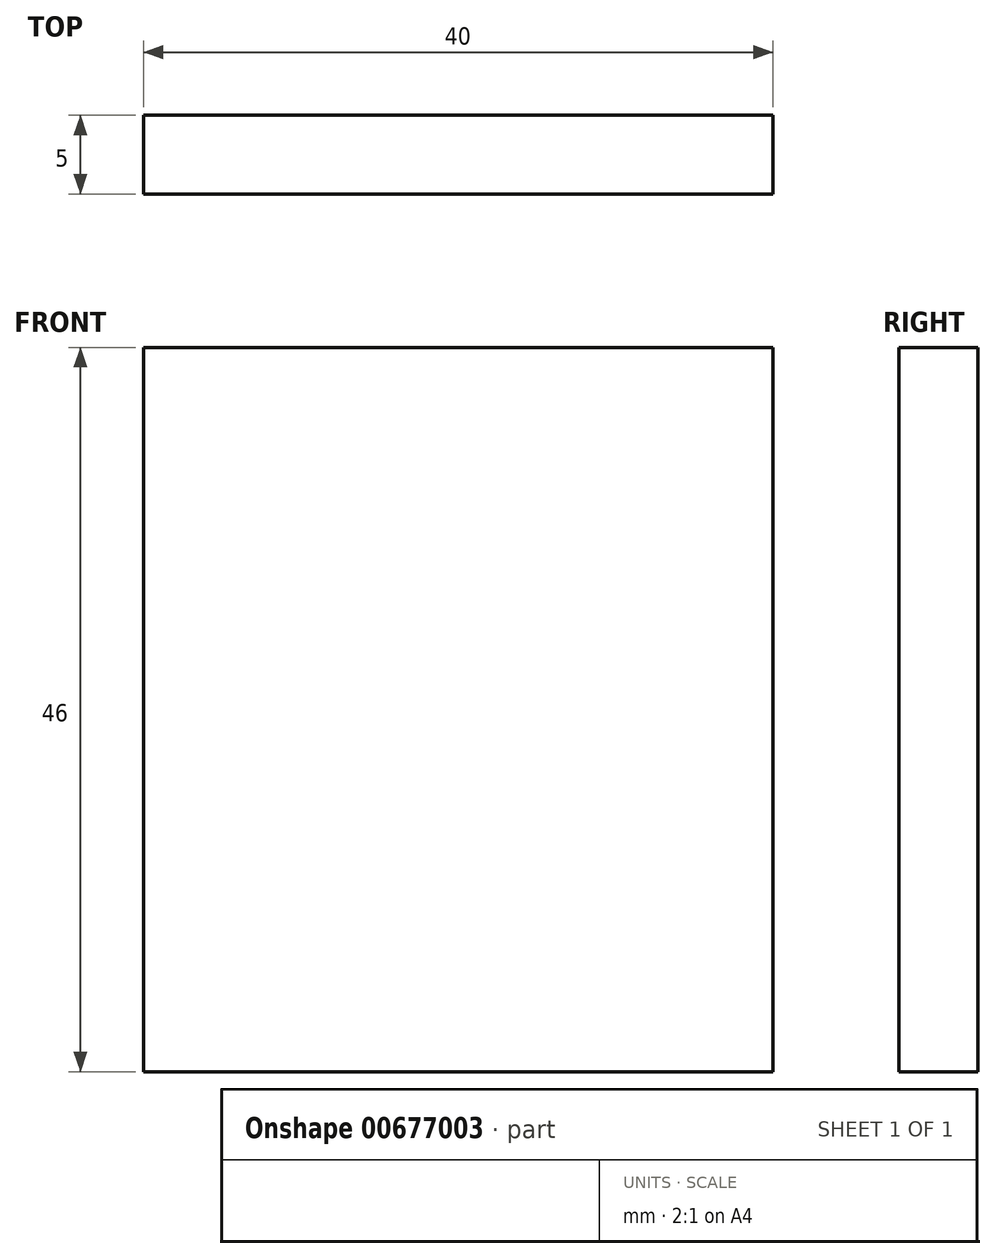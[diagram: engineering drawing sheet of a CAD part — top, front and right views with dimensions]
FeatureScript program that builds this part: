
annotation { "Feature Type Name" : "Feature", "Feature Type Description" : "" }
export const myFeature = defineFeature(function(context is Context, id is Id, definition is map)
    precondition{}
    {
        {
            var Q0;
            Q0=qCreatedBy(makeId("Front.planeOp"),FACE);
            var sketch = newSketch(context, id + "F0", { "sketchPlane" : qUnion([Q0])});
            skLineSegment(sketch, "E0.bottom", {"start": v(-20, 23) * mm, "end": v(20, 23) * mm});
            skLineSegment(sketch, "E0.top", {"start": v(-20, -23) * mm, "end": v(20, -23) * mm});
            skLineSegment(sketch, "E0.left", {"start": v(-20, 23) * mm, "end": v(-20, -23) * mm});
            skLineSegment(sketch, "E0.right", {"start": v(20, 23) * mm, "end": v(20, -23) * mm});
            skPoint(sketch, "E0.middle", {"position": v(0, 0) * mm});
            skSolve(sketch);
        }
        {
            var Q0;
            Q0 = qSketchRegion(id + "F0", true);
            extrude(context, id + "F1", {"entities" : qUnion([Q0]), "depth" : 5 * mm, "offsetDistance" : 25 * mm});
        }
    });
